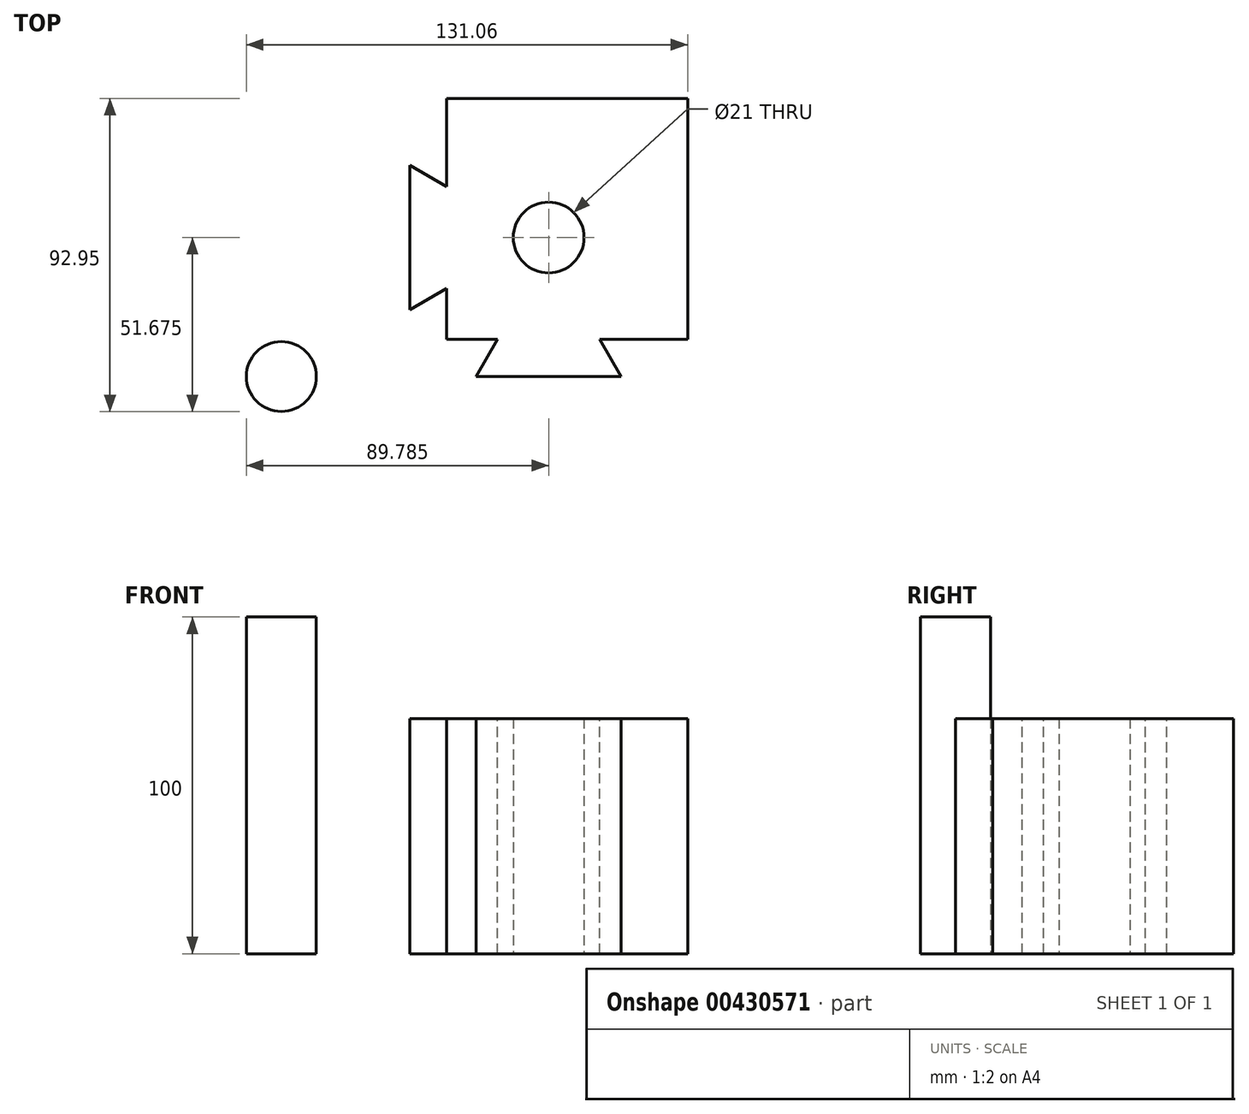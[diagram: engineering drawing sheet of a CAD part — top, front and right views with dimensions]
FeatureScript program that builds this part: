
annotation { "Feature Type Name" : "Feature", "Feature Type Description" : "" }
export const myFeature = defineFeature(function(context is Context, id is Id, definition is map)
    precondition{}
    {
        {
            var Q0;
            Q0=qCreatedBy(makeId("Top.planeOp"),FACE);
            var sketch = newSketch(context, id + "F0", { "sketchPlane" : qUnion([Q0])});
            skLineSegment(sketch, "E0.bottom", {"start": v(0, 0) * mm, "end": v(82.55, 0) * mm});
            skLineSegment(sketch, "E0.top", {"start": v(0, 82.55) * mm, "end": v(82.55, 82.55) * mm});
            skLineSegment(sketch, "E0.left", {"start": v(0, 0) * mm, "end": v(0, 82.55) * mm});
            skLineSegment(sketch, "E0.right", {"start": v(82.55, 0) * mm, "end": v(82.55, 82.55) * mm});
            skLineSegment(sketch, "E1", {"start": v(26.6, 41.27) * mm, "end": v(51.53, 41.27) * mm, "construction": true});
            skLineSegment(sketch, "E2", {"start": v(41.27, 49.49) * mm, "end": v(41.27, 28.63) * mm, "construction": true});
            skPoint(sketch, "E3", {"position": v(41.27, 41.27) * mm});
            skSolve(sketch);
        }
        {
            var Q0;
            Q0=makeQuery(id+"F0.imprint","IMPRINT",FACE,{"disambiguationData":[TD([[makeQuery(id+"F0.imprint","IMPRINT",EDGE,{"derivedFrom":sQuery(id+"F0.wireOp",EDGE,"E0.bottom")}),1.0]])]});
            extrude(context, id + "F1", {"entities" : qUnion([Q0]), "depth" : 69.85 * mm});
        }
        {
            var Q0;
            Q0=makeQuery(id+"F1.opExtrude","CAP_FACE",FACE,{"disambiguationData":[OSD([sQuery(id+"F0.wireOp",EDGE,"E0.bottom"),sQuery(id+"F0.wireOp",EDGE,"E0.top"),sQuery(id+"F0.wireOp",EDGE,"E0.left"),sQuery(id+"F0.wireOp",EDGE,"E0.right")])],"isStart":false});
            var sketch = newSketch(context, id + "F2", { "sketchPlane" : qUnion([Q0])});
            skLineSegment(sketch, "E4", {"start": v(0, 41.27) * mm, "end": v(24.23, 41.27) * mm, "construction": true});
            skLineSegment(sketch, "E5", {"start": v(11, 56.42) * mm, "end": v(0, 62.77) * mm});
            skLineSegment(sketch, "E6", {"start": v(0, 19.77) * mm, "end": v(11, 26.13) * mm});
            skLineSegment(sketch, "E7", {"start": v(11, 26.13) * mm, "end": v(11, 11) * mm});
            skLineSegment(sketch, "E8", {"start": v(11, 11) * mm, "end": v(11, 26.13) * mm});
            skLineSegment(sketch, "E9", {"start": v(11, 56.42) * mm, "end": v(11, 82.55) * mm});
            skLineSegment(sketch, "E10", {"start": v(11, 11) * mm, "end": v(82.55, 11) * mm});
            skLineSegment(sketch, "E11", {"start": v(41.27, 0) * mm, "end": v(41.27, 23.07) * mm, "construction": true});
            skPoint(sketch, "E11.endSnap0", {"position": v(41.27, 11) * mm});
            skLineSegment(sketch, "E12", {"start": v(19.77, 0) * mm, "end": v(26.13, 11) * mm});
            skLineSegment(sketch, "E13", {"start": v(62.77, 0) * mm, "end": v(56.42, 11) * mm});
            skSolve(sketch);
        }
        {
            var Q0;
            {var subQ0=sQuery(id+"F2.wireOp",EDGE,"E5");Q0=makeQuery(id+"F2.imprint","IMPRINT",FACE,{"disambiguationData":[TD([[makeQuery(id+"F2.imprint","IMPRINT",EDGE,{"derivedFrom":subQ0}),-1.0]])]});}
            var Q1;
            {var subQ0=sQuery(id+"F2.wireOp",EDGE,"E6");Q1=makeQuery(id+"F2.imprint","IMPRINT",FACE,{"disambiguationData":[TD([[makeQuery(id+"F2.imprint","IMPRINT",EDGE,{"derivedFrom":subQ0}),-1.0]])]});}
            var Q2;
            {var subQ3=sQuery(id+"F2.wireOp",EDGE,"E13");Q2=makeQuery(id+"F2.imprint","IMPRINT",FACE,{"disambiguationData":[TD([[makeQuery(id+"F2.imprint","IMPRINT",EDGE,{"derivedFrom":subQ3}),-1.0]])]});}
            extrude(context, id + "F3", {"entities" : qUnion([Q0, Q1, Q2]), "operationType" : NewBodyOperationType.REMOVE, "endBound" : BoundingType.UP_TO_NEXT, "oppositeDirection" : true, "depth" : 25 * mm});
        }
        {
            var Q0;
            Q0=sQuery(id+"F0.wireOp",VERTEX,"E3");
            var Q1;
            Q1=makeQuery(id+"F1.opExtrude","SWEPT_BODY",BODY,{"disambiguationData":[OSD([sQuery(id+"F0.wireOp",EDGE,"E0.bottom"),sQuery(id+"F0.wireOp",EDGE,"E0.top"),sQuery(id+"F0.wireOp",EDGE,"E0.left"),sQuery(id+"F0.wireOp",EDGE,"E0.right")])]});
            hole(context, id + "F4", {"style" : HoleStyle.SIMPLE, "endStyle" : HoleEndStyle.THROUGH, "oppositeDirection" : true, "standardTappedOrClearance" : lookupTablePath({ "standard" : "ISO", "fit" : "Close", "size" : "M20", "type" : "Clearance" }), "standardBlindInLast" : lookupTablePath({ "fit" : "Close", "standard" : "ISO", "size" : "M20", "type" : "Clearance" }), "holeDiameter" : 21 * mm, "isTappedThrough" : true, "tappedDepth" : 12 * mm, "tapClearance" : 3, "startFromSketch" : true, "locations" : qUnion([Q0]), "scope" : qUnion([Q1])});
        }
        {
            var Q0;
            Q0=qCreatedBy(makeId("Top.planeOp"),FACE);
            var sketch = newSketch(context, id + "F5", { "sketchPlane" : qUnion([Q0])});
            skCircle(sketch, "E14", {"center": v(-38.1, 0) * mm, "radius": 10.4 * mm});
            skSolve(sketch);
        }
        {
            var Q0;
            Q0=makeQuery(id+"F5.imprint","IMPRINT",FACE,{"disambiguationData":[TD([[makeQuery(id+"F5.imprint","IMPRINT",EDGE,{"derivedFrom":sQuery(id+"F5.wireOp",EDGE,"E14")}),1.0]])]});
            extrude(context, id + "F6", {"entities" : qUnion([Q0]), "depth" : 100 * mm});
        }
    });
